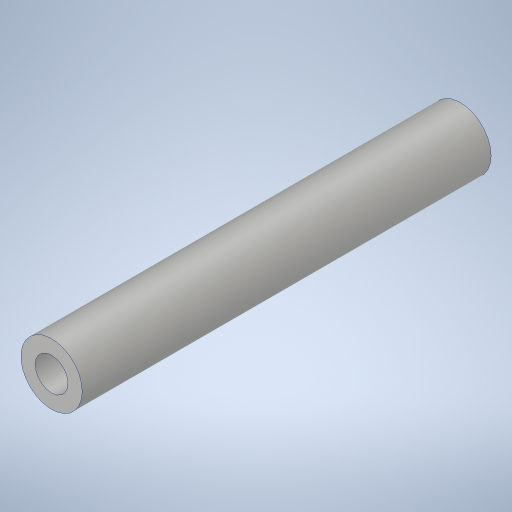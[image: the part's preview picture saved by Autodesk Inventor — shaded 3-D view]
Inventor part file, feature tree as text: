
AUTODESK INVENTOR PART (.ipt)
format: ipt  version: 2023.4 (Build 274418000, 418)  size: 238,592 bytes
history: native  units: in
note: dims shown in document units (in); Inventor stores cm internally (conversion verified against a paired STEP export)
features: extrude x1, hole x1
ambient origin geometry x8: Origin, YZ Plane, XZ Plane, XY Plane, X Axis, Y Axis, Z Axis, Center Point
bodies: Solid1 (feature_tree)
feature tree (2):
  extrude  "Extrusion1"  Depth=2.5in
  hole  "Hole1"  [1 undecoded]
note: 1 required parameter value undecoded (feature->parameter linkage not recoverable at this tier; creation-order binding heuristic only, values carry confidence <= 0.55)
